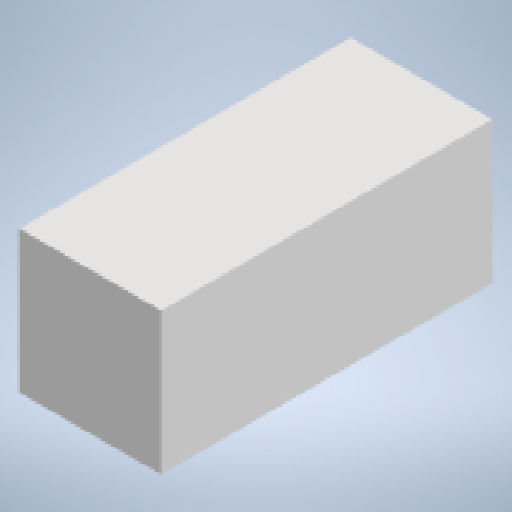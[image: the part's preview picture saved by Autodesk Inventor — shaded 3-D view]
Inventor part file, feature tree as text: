
AUTODESK INVENTOR PART (.ipt)
format: ipt  version: 2024 (Build 280153000, 153)  size: 160,256 bytes
history: native  units: in
note: dims shown in document units (in); Inventor stores cm internally (conversion verified against a paired STEP export)
features: chamfer x3, extrude x2, direct_edit x2, sketch x2, move_body x2, fillet x1
ambient origin geometry x8: Origin, YZ Plane, XZ Plane, XY Plane, X Axis, Y Axis, Z Axis, Center Point
bodies: Solid1 (feature_tree)
feature tree (12):
  extrude  "Extrusion1"  Depth=1.1811in
  extrude  "Extrusion2"  Depth=0.6496in
  chamfer  "Chamfer1"  Distance=0.3937in
  chamfer  "Chamfer3"  Distance=0.3937in Angle=60.0deg
  direct_edit  "Direct Edit1"
  direct_edit  "Direct Edit2"
  chamfer  "Chamfer4"  Distance=0.3937in Angle=60.0deg
  fillet  "Fillet1"  [1 undecoded]
  sketch  "Sketch1"  dims[d0=2.7559in d1=1.1811in]
  sketch  "Sketch2"  dims[d2=1.1811in d3=0.0in d4=0.6496in d5=0.3937in d6=0.0in d7=0.3937in d8=0.0787in d9=60.0deg d13=0.3937in d14=0.0787in d15=60.0deg d16=0.0in d17=0.0in d18=-0.3125in d19=0.0in d20=0.0in d21=-0.5118in d22=0.0787in d23=0.0787in d24=60.0deg d25=0.1969in]
  move_body  "Move1"
  move_body  "Move2"
note: 1 required parameter value undecoded (feature->parameter linkage not recoverable at this tier; creation-order binding heuristic only, values carry confidence <= 0.55)
